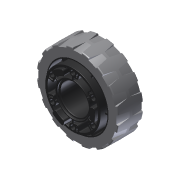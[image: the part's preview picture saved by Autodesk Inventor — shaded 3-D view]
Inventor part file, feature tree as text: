
AUTODESK INVENTOR PART (.ipt)
format: ipt  version: 2013 (Build 170138000, 138)  size: 3,077,120 bytes
history: native  units: in
note: dims shown in document units (in); Inventor stores cm internally (conversion verified against a paired STEP export)
features: imported_body x2, fillet x1, other x1, pattern_circular x1
ambient origin geometry x8: Origin, YZ Plane, XZ Plane, XY Plane, X Axis, Y Axis, Z Axis, Center Point
feature tree (5):
  fillet  "Fillet6"  [1 undecoded]
  other  "217-3202-STEP1"
  pattern_circular  "CirPattern6"
  imported_body  "Base1"
  imported_body  "Base2"
note: 1 required parameter value undecoded (feature->parameter linkage not recoverable at this tier; creation-order binding heuristic only, values carry confidence <= 0.55)
